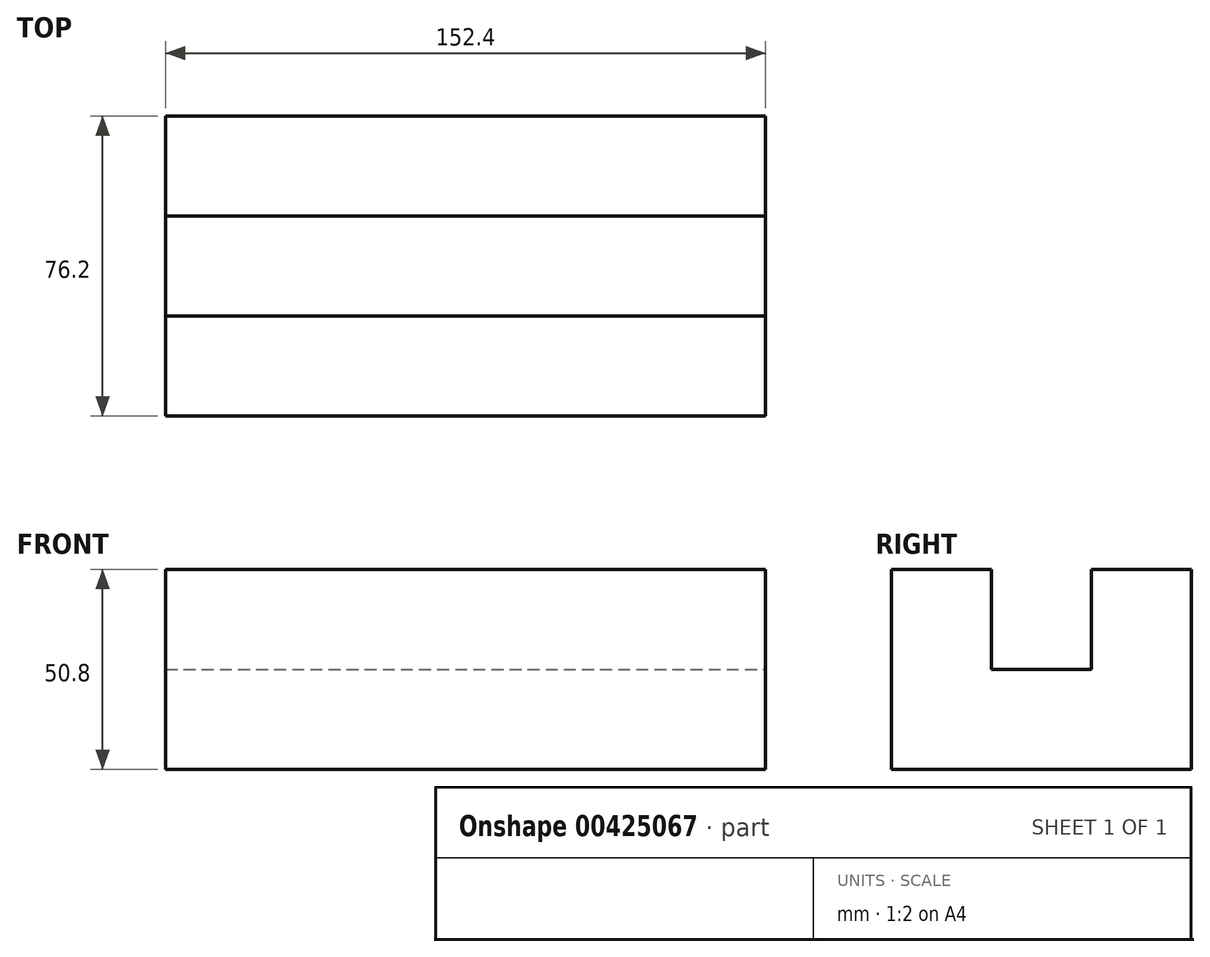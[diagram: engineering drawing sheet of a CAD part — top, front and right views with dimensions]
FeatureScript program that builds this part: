
annotation { "Feature Type Name" : "Feature", "Feature Type Description" : "" }
export const myFeature = defineFeature(function(context is Context, id is Id, definition is map)
    precondition{}
    {
        {
            var Q0;
            Q0=qCreatedBy(makeId("Front.planeOp"),FACE);
            var sketch = newSketch(context, id + "F0", { "sketchPlane" : qUnion([Q0])});
            skLineSegment(sketch, "E0", {"start": v(0, 0) * mm, "end": v(152.4, 0) * mm});
            skLineSegment(sketch, "E1", {"start": v(152.4, 0) * mm, "end": v(152.4, 50.8) * mm});
            skLineSegment(sketch, "E2", {"start": v(152.4, 50.8) * mm, "end": v(0, 50.8) * mm});
            skLineSegment(sketch, "E3", {"start": v(0, 50.8) * mm, "end": v(0, 0) * mm});
            skSolve(sketch);
        }
        {
            var Q0;
            Q0 = qSketchRegion(id + "F0", true);
            extrude(context, id + "F1", {"entities" : qUnion([Q0]), "depth" : 76.2 * mm});
        }
        {
            var Q0;
            Q0=makeQuery(id+"F1.opExtrude","SWEPT_FACE",FACE,{"disambiguationData":[OSD([sQuery(id+"F0.wireOp",EDGE,"E1")])]});
            var sketch = newSketch(context, id + "F2", { "sketchPlane" : qUnion([Q0])});
            skLineSegment(sketch, "E4", {"start": v(-76.2, 50.8) * mm, "end": v(-50.8, 50.8) * mm});
            skLineSegment(sketch, "E5", {"start": v(-50.8, 50.8) * mm, "end": v(-50.8, 25.4) * mm});
            skLineSegment(sketch, "E6", {"start": v(-50.8, 25.4) * mm, "end": v(-25.4, 25.4) * mm});
            skLineSegment(sketch, "E7", {"start": v(-25.4, 25.4) * mm, "end": v(-25.4, 50.8) * mm});
            skLineSegment(sketch, "E8", {"start": v(-25.4, 50.8) * mm, "end": v(0, 50.8) * mm});
            skSolve(sketch);
        }
        {
            var Q0;
            {var subQ0=sQuery(id+"F2.wireOp",EDGE,"E5");Q0=makeQuery(id+"F2.imprint","IMPRINT",FACE,{"disambiguationData":[TD([[makeQuery(id+"F2.imprint","IMPRINT",EDGE,{"derivedFrom":subQ0}),1.0]])]});}
            extrude(context, id + "F3", {"entities" : qUnion([Q0]), "operationType" : NewBodyOperationType.REMOVE, "oppositeDirection" : true, "depth" : 177.8 * mm});
        }
    });
